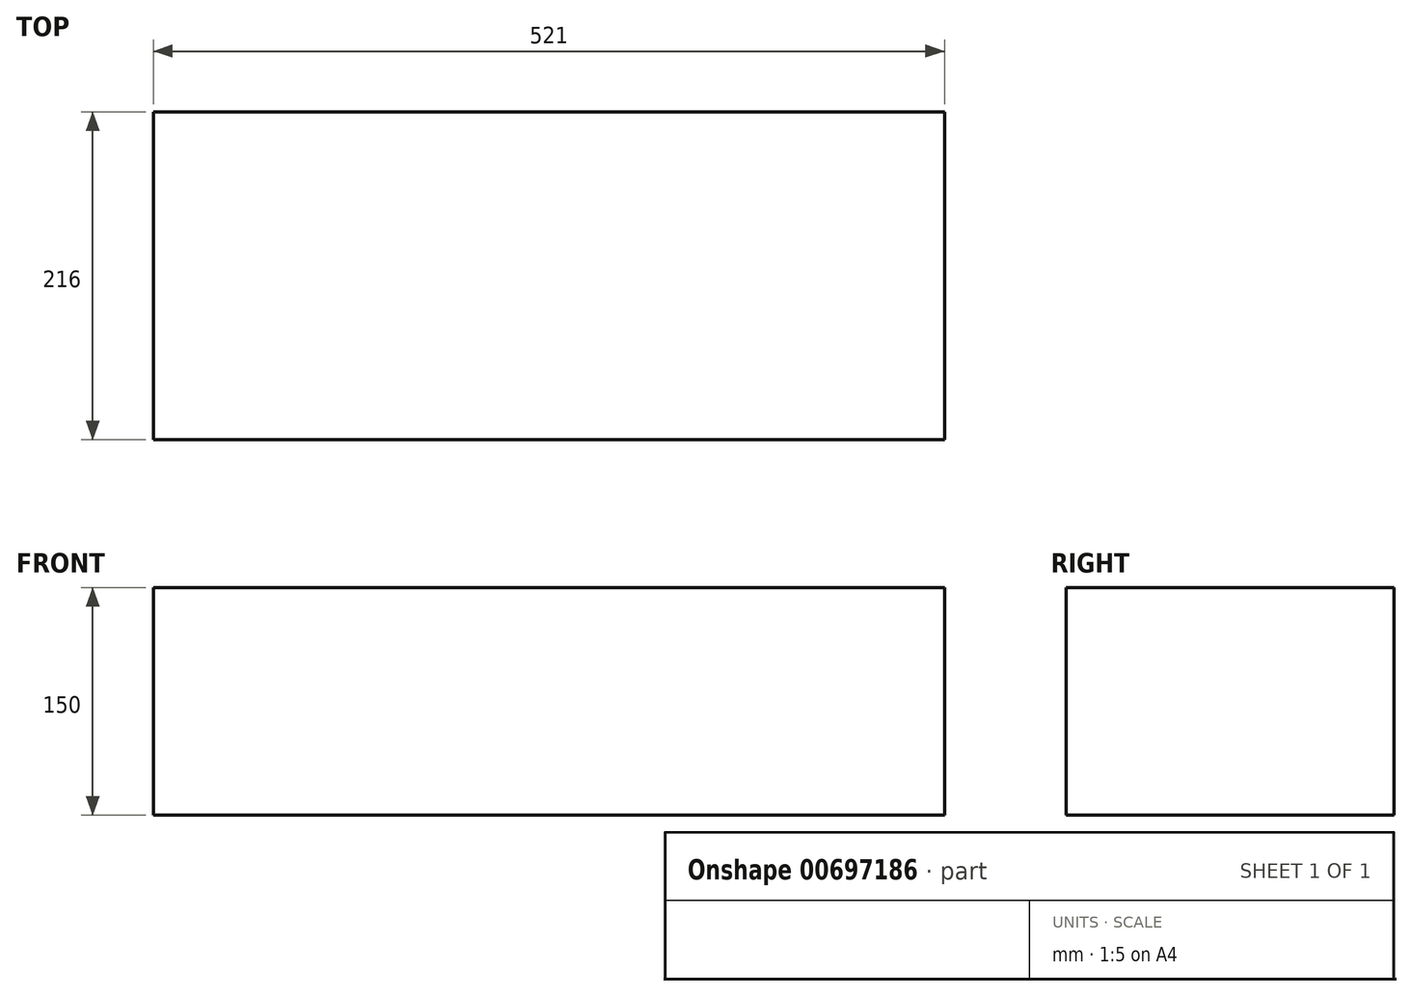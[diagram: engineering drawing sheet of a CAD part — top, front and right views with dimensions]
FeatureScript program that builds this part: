
annotation { "Feature Type Name" : "Feature", "Feature Type Description" : "" }
export const myFeature = defineFeature(function(context is Context, id is Id, definition is map)
    precondition{}
    {
        {
            var Q0;
            Q0=qCreatedBy(makeId("Top.planeOp"),FACE);
            var sketch = newSketch(context, id + "F0", { "sketchPlane" : qUnion([Q0])});
            skLineSegment(sketch, "E0.bottom", {"start": v(260.5, -108) * mm, "end": v(-260.5, -108) * mm});
            skLineSegment(sketch, "E0.top", {"start": v(260.5, 108) * mm, "end": v(-260.5, 108) * mm});
            skLineSegment(sketch, "E0.left", {"start": v(260.5, -108) * mm, "end": v(260.5, 108) * mm});
            skLineSegment(sketch, "E0.right", {"start": v(-260.5, -108) * mm, "end": v(-260.5, 108) * mm});
            skPoint(sketch, "E0.middle", {"position": v(0, 0) * mm});
            skSolve(sketch);
        }
        {
            var Q0;
            Q0=makeQuery(id+"F0.imprint","IMPRINT",FACE,{"disambiguationData":[TD([[makeQuery(id+"F0.imprint","IMPRINT",EDGE,{"derivedFrom":sQuery(id+"F0.wireOp",EDGE,"E0.bottom")}),-1.0]])]});
            extrude(context, id + "F1", {"entities" : qUnion([Q0]), "depth" : 150 * mm, "offsetDistance" : 25 * mm});
        }
    });
